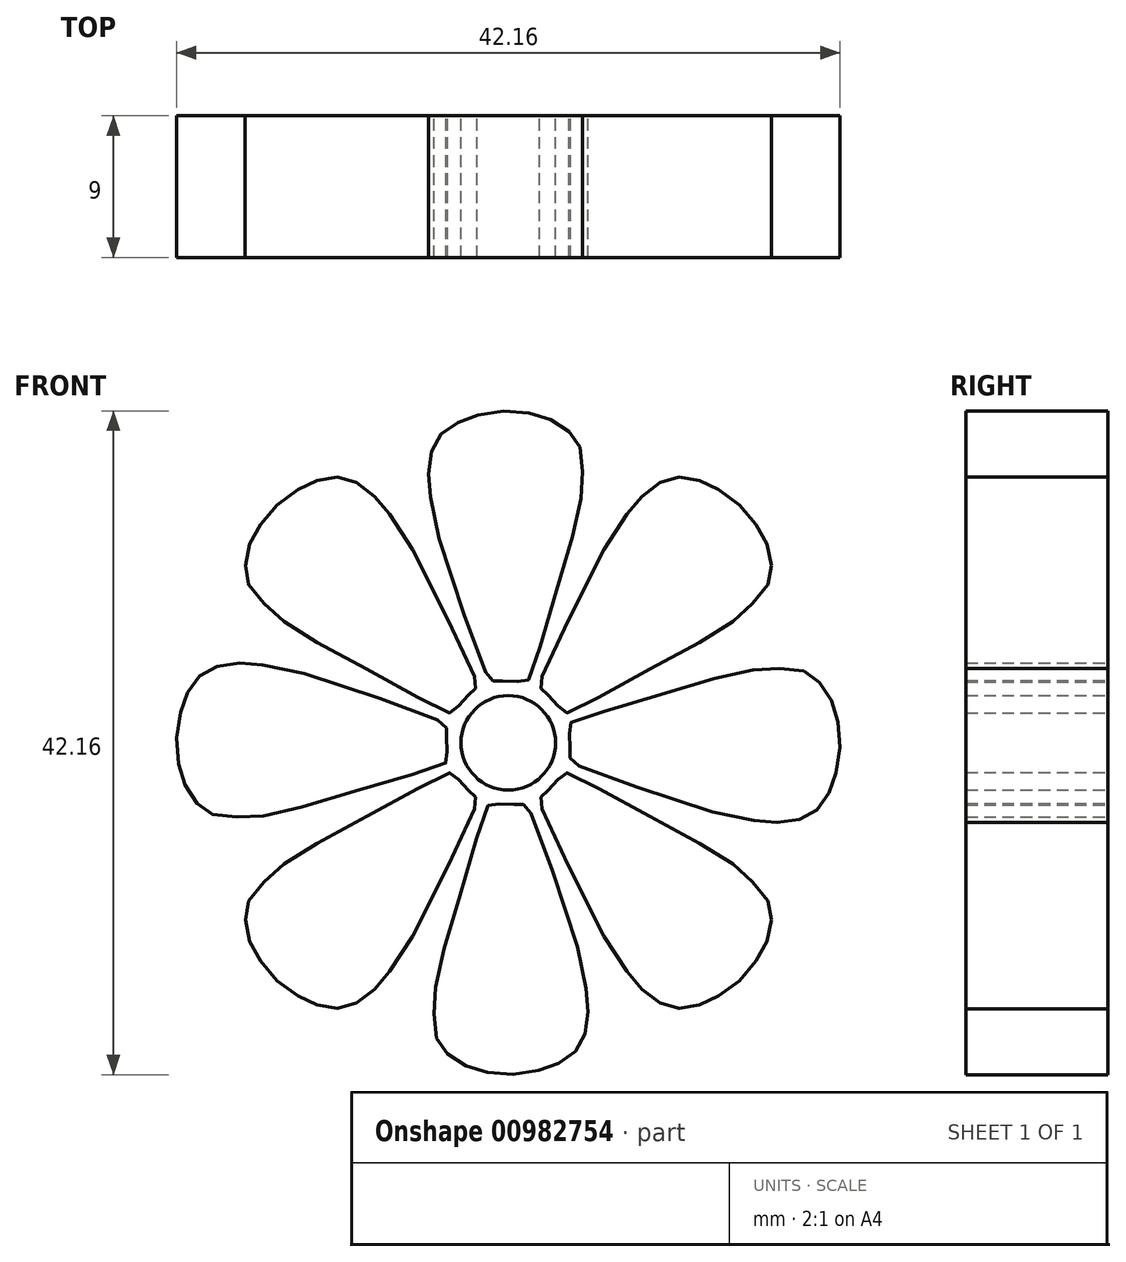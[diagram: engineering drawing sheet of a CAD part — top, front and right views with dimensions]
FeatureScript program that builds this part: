
annotation { "Feature Type Name" : "Feature", "Feature Type Description" : "" }
export const myFeature = defineFeature(function(context is Context, id is Id, definition is map)
    precondition{}
    {
        {
            var Q0;
            Q0=qCreatedBy(makeId("Front.planeOp"),FACE);
            var sketch = newSketch(context, id + "F0", { "sketchPlane" : qUnion([Q0])});
            skCircle(sketch, "E0", {"center": v(0, 0) * mm, "radius": 3 * mm});
            skFitSpline(sketch, "E1", {"points": [v(-0.96, 3.92) * mm, v(-1.11, 4) * mm, v(-1.38, 4.47) * mm, v(-4.52, 14) * mm, v(-4.97, 16.21) * mm, v(-5.03, 17.24) * mm, v(-4.88, 18.3) * mm, v(-4.52, 19.15) * mm, v(-4.1, 19.72) * mm, v(-3.37, 20.24) * mm, v(-2.55, 20.6) * mm, v(-1.5, 20.87) * mm, v(0, 21.02) * mm, v(1.35, 20.9) * mm, v(2.35, 20.63) * mm, v(3.32, 20.14) * mm, v(3.99, 19.6) * mm, v(4.4, 19) * mm, v(4.65, 17.94) * mm, v(4.68, 16.6) * mm, v(4.44, 14.88) * mm, v(2.84, 9.01) * mm, v(1.3, 4.1) * mm, v(1.14, 3.88) * mm, v(1.01, 3.86) * mm, v(0.6, 3.9) * mm, v(0, 3.94) * mm, v(-0.36, 3.93) * mm, v(-0.67, 3.9) * mm, v(-0.9, 3.9) * mm, v(-0.96, 3.92) * mm]});
            skLineSegment(sketch, "E2", {"start": v(0, 21.02) * mm, "end": v(0, 0) * mm, "construction": true});
            skCircle(sketch, "E3", {"center": v(0, 0) * mm, "radius": 21.02 * mm, "construction": true});
            skLineSegment(sketch, "E4.1.0", {"start": v(-14.87, 14.87) * mm, "end": v(0, 0) * mm, "construction": true});
            skLineSegment(sketch, "E4.2.0", {"start": v(-21.02, 0) * mm, "end": v(0, 0) * mm, "construction": true});
            skLineSegment(sketch, "E4.3.0", {"start": v(-14.87, -14.87) * mm, "end": v(0, 0) * mm, "construction": true});
            skLineSegment(sketch, "E4.4.0", {"start": v(0, -21.02) * mm, "end": v(0, 0) * mm, "construction": true});
            skLineSegment(sketch, "E4.5.0", {"start": v(14.87, -14.87) * mm, "end": v(0, 0) * mm, "construction": true});
            skLineSegment(sketch, "E4.6.0", {"start": v(21.02, 0) * mm, "end": v(0, 0) * mm, "construction": true});
            skLineSegment(sketch, "E4.7.0", {"start": v(14.87, 14.87) * mm, "end": v(0, 0) * mm, "construction": true});
            skFitSpline(sketch, "E5", {"points": [v(2.1, 3.45) * mm, v(2.04, 3.61) * mm, v(2.18, 4.13) * mm, v(6.7, 13.1) * mm, v(7.95, 14.98) * mm, v(8.63, 15.75) * mm, v(9.49, 16.39) * mm, v(10.35, 16.73) * mm, v(11.05, 16.84) * mm, v(11.93, 16.69) * mm, v(12.76, 16.37) * mm, v(13.7, 15.81) * mm, v(14.87, 14.87) * mm, v(15.74, 13.82) * mm, v(16.25, 12.92) * mm, v(16.6, 11.9) * mm, v(16.68, 11.04) * mm, v(16.55, 10.31) * mm, v(15.97, 9.4) * mm, v(15.05, 8.43) * mm, v(13.66, 7.38) * mm, v(8.38, 4.37) * mm, v(3.82, 2) * mm, v(3.55, 1.93) * mm, v(3.45, 2.02) * mm, v(3.17, 2.33) * mm, v(2.79, 2.79) * mm, v(2.52, 3.03) * mm, v(2.29, 3.23) * mm, v(2.13, 3.4) * mm, v(2.1, 3.45) * mm]});
            skFitSpline(sketch, "E6.MirrorC", {"points": [v(-3.92, 0.96) * mm, v(-4, 1.11) * mm, v(-4.47, 1.38) * mm, v(-14, 4.52) * mm, v(-16.21, 4.97) * mm, v(-17.24, 5.03) * mm, v(-18.3, 4.88) * mm, v(-19.15, 4.52) * mm, v(-19.72, 4.1) * mm, v(-20.24, 3.37) * mm, v(-20.6, 2.55) * mm, v(-20.87, 1.5) * mm, v(-21.02, 0) * mm, v(-20.9, -1.35) * mm, v(-20.63, -2.35) * mm, v(-20.14, -3.32) * mm, v(-19.6, -3.99) * mm, v(-19, -4.4) * mm, v(-17.94, -4.65) * mm, v(-16.6, -4.68) * mm, v(-14.88, -4.44) * mm, v(-9.01, -2.84) * mm, v(-4.1, -1.3) * mm, v(-3.88, -1.14) * mm, v(-3.86, -1.01) * mm, v(-3.9, -0.6) * mm, v(-3.94, 0) * mm, v(-3.93, 0.36) * mm, v(-3.9, 0.67) * mm, v(-3.9, 0.9) * mm, v(-3.92, 0.96) * mm]});
            skFitSpline(sketch, "E7.MirrorC", {"points": [v(0.96, -3.92) * mm, v(1.11, -4) * mm, v(1.38, -4.47) * mm, v(4.52, -14) * mm, v(4.97, -16.21) * mm, v(5.03, -17.24) * mm, v(4.88, -18.3) * mm, v(4.52, -19.15) * mm, v(4.1, -19.72) * mm, v(3.37, -20.24) * mm, v(2.55, -20.6) * mm, v(1.5, -20.87) * mm, v(0, -21.02) * mm, v(-1.35, -20.9) * mm, v(-2.35, -20.63) * mm, v(-3.32, -20.14) * mm, v(-3.99, -19.6) * mm, v(-4.4, -19) * mm, v(-4.65, -17.94) * mm, v(-4.68, -16.6) * mm, v(-4.44, -14.88) * mm, v(-2.84, -9.01) * mm, v(-1.3, -4.1) * mm, v(-1.14, -3.88) * mm, v(-1.01, -3.86) * mm, v(-0.6, -3.9) * mm, v(0, -3.94) * mm, v(0.36, -3.93) * mm, v(0.67, -3.9) * mm, v(0.9, -3.9) * mm, v(0.96, -3.92) * mm]});
            skFitSpline(sketch, "E8.MirrorC", {"points": [v(3.92, -0.96) * mm, v(4, -1.11) * mm, v(4.47, -1.38) * mm, v(14, -4.52) * mm, v(16.21, -4.97) * mm, v(17.24, -5.03) * mm, v(18.3, -4.88) * mm, v(19.15, -4.52) * mm, v(19.72, -4.1) * mm, v(20.24, -3.37) * mm, v(20.6, -2.55) * mm, v(20.87, -1.5) * mm, v(21.02, 0) * mm, v(20.9, 1.35) * mm, v(20.63, 2.35) * mm, v(20.14, 3.32) * mm, v(19.6, 3.99) * mm, v(19, 4.4) * mm, v(17.94, 4.65) * mm, v(16.6, 4.68) * mm, v(14.88, 4.44) * mm, v(9.01, 2.84) * mm, v(4.1, 1.3) * mm, v(3.88, 1.14) * mm, v(3.86, 1.01) * mm, v(3.9, 0.6) * mm, v(3.94, 0) * mm, v(3.93, -0.36) * mm, v(3.9, -0.67) * mm, v(3.9, -0.9) * mm, v(3.92, -0.96) * mm]});
            skFitSpline(sketch, "E9.MirrorC", {"points": [v(2.1, -3.45) * mm, v(2.04, -3.61) * mm, v(2.18, -4.13) * mm, v(6.7, -13.1) * mm, v(7.95, -14.98) * mm, v(8.63, -15.75) * mm, v(9.49, -16.39) * mm, v(10.35, -16.73) * mm, v(11.05, -16.84) * mm, v(11.93, -16.69) * mm, v(12.76, -16.37) * mm, v(13.7, -15.81) * mm, v(14.87, -14.87) * mm, v(15.74, -13.82) * mm, v(16.25, -12.92) * mm, v(16.6, -11.9) * mm, v(16.68, -11.04) * mm, v(16.55, -10.31) * mm, v(15.97, -9.4) * mm, v(15.05, -8.43) * mm, v(13.66, -7.38) * mm, v(8.38, -4.37) * mm, v(3.82, -2) * mm, v(3.55, -1.93) * mm, v(3.45, -2.02) * mm, v(3.17, -2.33) * mm, v(2.79, -2.79) * mm, v(2.52, -3.03) * mm, v(2.29, -3.23) * mm, v(2.13, -3.4) * mm, v(2.1, -3.45) * mm]});
            skFitSpline(sketch, "E10.MirrorC", {"points": [v(-2.1, 3.45) * mm, v(-2.04, 3.61) * mm, v(-2.18, 4.13) * mm, v(-6.7, 13.1) * mm, v(-7.95, 14.98) * mm, v(-8.63, 15.75) * mm, v(-9.49, 16.39) * mm, v(-10.35, 16.73) * mm, v(-11.05, 16.84) * mm, v(-11.93, 16.69) * mm, v(-12.76, 16.37) * mm, v(-13.7, 15.81) * mm, v(-14.87, 14.87) * mm, v(-15.74, 13.82) * mm, v(-16.25, 12.92) * mm, v(-16.6, 11.9) * mm, v(-16.68, 11.04) * mm, v(-16.55, 10.31) * mm, v(-15.97, 9.4) * mm, v(-15.05, 8.43) * mm, v(-13.66, 7.38) * mm, v(-8.38, 4.37) * mm, v(-3.82, 2) * mm, v(-3.55, 1.93) * mm, v(-3.45, 2.02) * mm, v(-3.17, 2.33) * mm, v(-2.79, 2.79) * mm, v(-2.52, 3.03) * mm, v(-2.29, 3.23) * mm, v(-2.13, 3.4) * mm, v(-2.1, 3.45) * mm]});
            skFitSpline(sketch, "E11.MirrorC", {"points": [v(-2.1, -3.45) * mm, v(-2.04, -3.61) * mm, v(-2.18, -4.13) * mm, v(-6.7, -13.1) * mm, v(-7.95, -14.98) * mm, v(-8.63, -15.75) * mm, v(-9.49, -16.39) * mm, v(-10.35, -16.73) * mm, v(-11.05, -16.84) * mm, v(-11.93, -16.69) * mm, v(-12.76, -16.37) * mm, v(-13.7, -15.81) * mm, v(-14.87, -14.87) * mm, v(-15.74, -13.82) * mm, v(-16.25, -12.92) * mm, v(-16.6, -11.9) * mm, v(-16.68, -11.04) * mm, v(-16.55, -10.31) * mm, v(-15.97, -9.4) * mm, v(-15.05, -8.43) * mm, v(-13.66, -7.38) * mm, v(-8.38, -4.37) * mm, v(-3.82, -2) * mm, v(-3.55, -1.93) * mm, v(-3.45, -2.02) * mm, v(-3.17, -2.33) * mm, v(-2.79, -2.79) * mm, v(-2.52, -3.03) * mm, v(-2.29, -3.23) * mm, v(-2.13, -3.4) * mm, v(-2.1, -3.45) * mm]});
            skCircle(sketch, "E12", {"center": v(0, 0) * mm, "radius": 26.5 * mm});
            skSolve(sketch);
        }
        {
            var Q0;
            Q0=qCreatedBy(makeId("Front.planeOp"),FACE);
            var sketch = newSketch(context, id + "F1", { "sketchPlane" : qUnion([Q0])});
            skFitSpline(sketch, "E13.0", {"points": [v(-2.1, 3.45) * mm, v(-2.08, 3.49) * mm, v(-2, 3.66) * mm, v(-2.16, 4.25) * mm, v(-6.67, 13.33) * mm, v(-7.84, 14.86) * mm, v(-8.6, 15.77) * mm, v(-9.45, 16.43) * mm, v(-10.34, 16.75) * mm, v(-11.05, 16.9) * mm, v(-11.95, 16.7) * mm, v(-12.79, 16.39) * mm, v(-13.74, 15.83) * mm, v(-14.9, 14.9) * mm, v(-15.76, 13.85) * mm, v(-16.28, 12.95) * mm, v(-16.63, 11.91) * mm, v(-16.7, 11.04) * mm, v(-16.61, 10.28) * mm, v(-15.98, 9.35) * mm, v(-15.02, 8.36) * mm, v(-13.56, 7.22) * mm, v(-8.62, 4.48) * mm, v(-3.99, 2) * mm, v(-3.55, 1.9) * mm, v(-3.44, 2.03) * mm, v(-3.16, 2.35) * mm, v(-2.8, 2.8) * mm, v(-2.53, 3.03) * mm, v(-2.3, 3.22) * mm, v(-2.12, 3.39) * mm, v(-2.1, 3.43) * mm, v(-2.1, 3.45) * mm]});
            skFitSpline(sketch, "E14.0", {"points": [v(-3.92, 0.96) * mm, v(-3.93, 1) * mm, v(-4, 1.17) * mm, v(-4.53, 1.47) * mm, v(-14.14, 4.71) * mm, v(-16.05, 4.96) * mm, v(-17.24, 5.07) * mm, v(-18.3, 4.93) * mm, v(-19.15, 4.54) * mm, v(-19.76, 4.13) * mm, v(-20.27, 3.37) * mm, v(-20.63, 2.54) * mm, v(-20.9, 1.48) * mm, v(-21.08, 0) * mm, v(-20.93, -1.35) * mm, v(-20.67, -2.35) * mm, v(-20.18, -3.33) * mm, v(-19.62, -4) * mm, v(-19.01, -4.48) * mm, v(-17.91, -4.7) * mm, v(-16.53, -4.71) * mm, v(-14.7, -4.48) * mm, v(-9.27, -2.93) * mm, v(-4.23, -1.4) * mm, v(-3.86, -1.16) * mm, v(-3.86, -1) * mm, v(-3.9, -0.58) * mm, v(-3.95, 0) * mm, v(-3.93, 0.35) * mm, v(-3.9, 0.65) * mm, v(-3.9, 0.9) * mm, v(-3.9, 0.93) * mm, v(-3.92, 0.96) * mm]});
            skFitSpline(sketch, "E15.0", {"points": [v(-0.96, 3.92) * mm, v(-1, 3.93) * mm, v(-1.17, 4) * mm, v(-1.47, 4.53) * mm, v(-4.71, 14.14) * mm, v(-4.96, 16.05) * mm, v(-5.07, 17.24) * mm, v(-4.93, 18.3) * mm, v(-4.54, 19.15) * mm, v(-4.13, 19.76) * mm, v(-3.37, 20.27) * mm, v(-2.54, 20.63) * mm, v(-1.48, 20.9) * mm, v(0, 21.08) * mm, v(1.35, 20.93) * mm, v(2.35, 20.67) * mm, v(3.33, 20.18) * mm, v(4, 19.62) * mm, v(4.48, 19.01) * mm, v(4.7, 17.91) * mm, v(4.71, 16.53) * mm, v(4.48, 14.7) * mm, v(2.93, 9.27) * mm, v(1.4, 4.23) * mm, v(1.16, 3.86) * mm, v(1, 3.86) * mm, v(0.58, 3.9) * mm, v(0, 3.95) * mm, v(-0.35, 3.93) * mm, v(-0.65, 3.9) * mm, v(-0.9, 3.9) * mm, v(-0.93, 3.9) * mm, v(-0.96, 3.92) * mm]});
            skFitSpline(sketch, "E16.0", {"points": [v(2.1, 3.45) * mm, v(2.08, 3.49) * mm, v(2, 3.66) * mm, v(2.16, 4.25) * mm, v(6.67, 13.33) * mm, v(7.84, 14.86) * mm, v(8.6, 15.77) * mm, v(9.45, 16.43) * mm, v(10.34, 16.75) * mm, v(11.05, 16.9) * mm, v(11.95, 16.7) * mm, v(12.79, 16.39) * mm, v(13.74, 15.83) * mm, v(14.9, 14.9) * mm, v(15.76, 13.85) * mm, v(16.28, 12.95) * mm, v(16.63, 11.91) * mm, v(16.7, 11.04) * mm, v(16.61, 10.28) * mm, v(15.98, 9.35) * mm, v(15.02, 8.36) * mm, v(13.56, 7.22) * mm, v(8.62, 4.48) * mm, v(3.99, 2) * mm, v(3.55, 1.9) * mm, v(3.44, 2.03) * mm, v(3.16, 2.35) * mm, v(2.8, 2.8) * mm, v(2.53, 3.03) * mm, v(2.3, 3.22) * mm, v(2.12, 3.39) * mm, v(2.1, 3.43) * mm, v(2.1, 3.45) * mm]});
            skFitSpline(sketch, "E17.0", {"points": [v(3.92, -0.96) * mm, v(3.93, -1) * mm, v(4, -1.17) * mm, v(4.53, -1.47) * mm, v(14.14, -4.71) * mm, v(16.05, -4.96) * mm, v(17.24, -5.07) * mm, v(18.3, -4.93) * mm, v(19.15, -4.54) * mm, v(19.76, -4.13) * mm, v(20.27, -3.37) * mm, v(20.63, -2.54) * mm, v(20.9, -1.48) * mm, v(21.08, 0) * mm, v(20.93, 1.35) * mm, v(20.67, 2.35) * mm, v(20.18, 3.33) * mm, v(19.62, 4) * mm, v(19.01, 4.48) * mm, v(17.91, 4.7) * mm, v(16.53, 4.71) * mm, v(14.7, 4.48) * mm, v(9.27, 2.93) * mm, v(4.23, 1.4) * mm, v(3.86, 1.16) * mm, v(3.86, 1) * mm, v(3.9, 0.58) * mm, v(3.95, 0) * mm, v(3.93, -0.35) * mm, v(3.9, -0.65) * mm, v(3.9, -0.9) * mm, v(3.9, -0.93) * mm, v(3.92, -0.96) * mm]});
            skFitSpline(sketch, "E18.0", {"points": [v(2.1, -3.45) * mm, v(2.08, -3.49) * mm, v(2, -3.66) * mm, v(2.16, -4.25) * mm, v(6.67, -13.33) * mm, v(7.84, -14.86) * mm, v(8.6, -15.77) * mm, v(9.45, -16.43) * mm, v(10.34, -16.75) * mm, v(11.05, -16.9) * mm, v(11.95, -16.7) * mm, v(12.79, -16.39) * mm, v(13.74, -15.83) * mm, v(14.9, -14.9) * mm, v(15.76, -13.85) * mm, v(16.28, -12.95) * mm, v(16.63, -11.91) * mm, v(16.7, -11.04) * mm, v(16.61, -10.28) * mm, v(15.98, -9.35) * mm, v(15.02, -8.36) * mm, v(13.56, -7.22) * mm, v(8.62, -4.48) * mm, v(3.99, -2) * mm, v(3.55, -1.9) * mm, v(3.44, -2.03) * mm, v(3.16, -2.35) * mm, v(2.8, -2.8) * mm, v(2.53, -3.03) * mm, v(2.3, -3.22) * mm, v(2.12, -3.39) * mm, v(2.1, -3.43) * mm, v(2.1, -3.45) * mm]});
            skFitSpline(sketch, "E19.0", {"points": [v(0.96, -3.92) * mm, v(1, -3.93) * mm, v(1.17, -4) * mm, v(1.47, -4.53) * mm, v(4.71, -14.14) * mm, v(4.96, -16.05) * mm, v(5.07, -17.24) * mm, v(4.93, -18.3) * mm, v(4.54, -19.15) * mm, v(4.13, -19.76) * mm, v(3.37, -20.27) * mm, v(2.54, -20.63) * mm, v(1.48, -20.9) * mm, v(0, -21.08) * mm, v(-1.35, -20.93) * mm, v(-2.35, -20.67) * mm, v(-3.33, -20.18) * mm, v(-4, -19.62) * mm, v(-4.48, -19.01) * mm, v(-4.7, -17.91) * mm, v(-4.71, -16.53) * mm, v(-4.48, -14.7) * mm, v(-2.93, -9.27) * mm, v(-1.4, -4.23) * mm, v(-1.16, -3.86) * mm, v(-1, -3.86) * mm, v(-0.58, -3.9) * mm, v(0, -3.95) * mm, v(0.35, -3.93) * mm, v(0.65, -3.9) * mm, v(0.9, -3.9) * mm, v(0.93, -3.9) * mm, v(0.96, -3.92) * mm]});
            skFitSpline(sketch, "E20.0", {"points": [v(-2.1, -3.45) * mm, v(-2.08, -3.49) * mm, v(-2, -3.66) * mm, v(-2.16, -4.25) * mm, v(-6.67, -13.33) * mm, v(-7.84, -14.86) * mm, v(-8.6, -15.77) * mm, v(-9.45, -16.43) * mm, v(-10.34, -16.75) * mm, v(-11.05, -16.9) * mm, v(-11.95, -16.7) * mm, v(-12.79, -16.39) * mm, v(-13.74, -15.83) * mm, v(-14.9, -14.9) * mm, v(-15.76, -13.85) * mm, v(-16.28, -12.95) * mm, v(-16.63, -11.91) * mm, v(-16.7, -11.04) * mm, v(-16.61, -10.28) * mm, v(-15.98, -9.35) * mm, v(-15.02, -8.36) * mm, v(-13.56, -7.22) * mm, v(-8.62, -4.48) * mm, v(-3.99, -2) * mm, v(-3.55, -1.9) * mm, v(-3.44, -2.03) * mm, v(-3.16, -2.35) * mm, v(-2.8, -2.8) * mm, v(-2.53, -3.03) * mm, v(-2.3, -3.22) * mm, v(-2.12, -3.39) * mm, v(-2.1, -3.43) * mm, v(-2.1, -3.45) * mm]});
            skCircle(sketch, "E21.0", {"center": v(0, 0) * mm, "radius": 3 * mm});
            skSolve(sketch);
        }
        {
            var Q0;
            Q0=makeQuery(id+"F1.imprint","IMPRINT",FACE,{"disambiguationData":[TD([[makeQuery(id+"F1.imprint","IMPRINT",EDGE,{"derivedFrom":sQuery(id+"F1.wireOp",EDGE,"E13.0")}),1.0]])]});
            var Q1;
            Q1=makeQuery(id+"F1.imprint","IMPRINT",FACE,{"disambiguationData":[TD([[makeQuery(id+"F1.imprint","IMPRINT",EDGE,{"derivedFrom":sQuery(id+"F1.wireOp",EDGE,"E15.0")}),-1.0]])]});
            var Q2;
            Q2=makeQuery(id+"F1.imprint","IMPRINT",FACE,{"disambiguationData":[TD([[makeQuery(id+"F1.imprint","IMPRINT",EDGE,{"derivedFrom":sQuery(id+"F1.wireOp",EDGE,"E16.0")}),-1.0]])]});
            var Q3;
            Q3=makeQuery(id+"F1.imprint","IMPRINT",FACE,{"disambiguationData":[TD([[makeQuery(id+"F1.imprint","IMPRINT",EDGE,{"derivedFrom":sQuery(id+"F1.wireOp",EDGE,"E17.0")}),1.0]])]});
            var Q4;
            Q4=makeQuery(id+"F1.imprint","IMPRINT",FACE,{"disambiguationData":[TD([[makeQuery(id+"F1.imprint","IMPRINT",EDGE,{"derivedFrom":sQuery(id+"F1.wireOp",EDGE,"E18.0")}),1.0]])]});
            var Q5;
            Q5=makeQuery(id+"F1.imprint","IMPRINT",FACE,{"disambiguationData":[TD([[makeQuery(id+"F1.imprint","IMPRINT",EDGE,{"derivedFrom":sQuery(id+"F1.wireOp",EDGE,"E19.0")}),-1.0]])]});
            var Q6;
            Q6=makeQuery(id+"F1.imprint","IMPRINT",FACE,{"disambiguationData":[TD([[makeQuery(id+"F1.imprint","IMPRINT",EDGE,{"derivedFrom":sQuery(id+"F1.wireOp",EDGE,"E20.0")}),-1.0]])]});
            var Q7;
            Q7=makeQuery(id+"F1.imprint","IMPRINT",FACE,{"disambiguationData":[TD([[makeQuery(id+"F1.imprint","IMPRINT",EDGE,{"derivedFrom":sQuery(id+"F1.wireOp",EDGE,"E14.0")}),1.0]])]});
            var Q8;
            Q8=makeQuery(id+"F1.imprint","IMPRINT",FACE,{"disambiguationData":[TD([[makeQuery(id+"F1.imprint","IMPRINT",EDGE,{"derivedFrom":sQuery(id+"F1.wireOp",EDGE,"E21.0")}),1.0]])]});
            extrude(context, id + "F2", {"entities" : qUnion([Q0, Q1, Q2, Q3, Q4, Q5, Q6, Q7, Q8]), "endBound" : BoundingType.SYMMETRIC, "depth" : 9 * mm, "offsetDistance" : 25 * mm});
        }
    });
